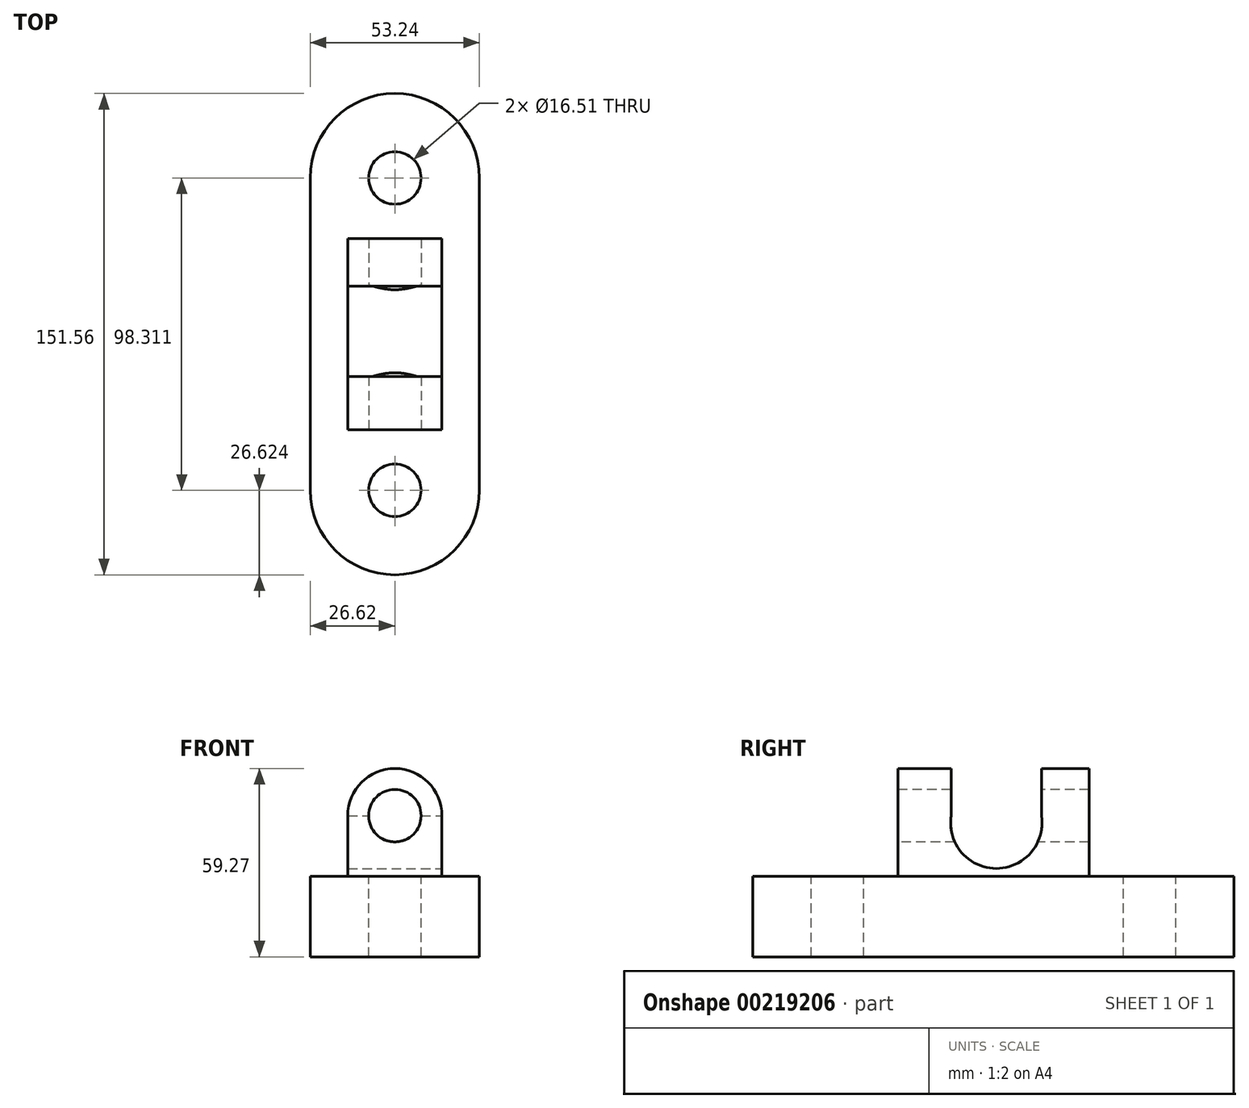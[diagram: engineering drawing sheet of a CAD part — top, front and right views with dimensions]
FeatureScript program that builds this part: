
annotation { "Feature Type Name" : "Feature", "Feature Type Description" : "" }
export const myFeature = defineFeature(function(context is Context, id is Id, definition is map)
    precondition{}
    {
        {
            var Q0;
            Q0=qCreatedBy(makeId("Top.planeOp"),FACE);
            var sketch = newSketch(context, id + "F0", { "sketchPlane" : qUnion([Q0])});
            skLineSegment(sketch, "E0.left", {"start": v(26.62, 49.16) * mm, "end": v(26.62, -49.16) * mm});
            skLineSegment(sketch, "E0.right", {"start": v(-26.62, 49.16) * mm, "end": v(-26.62, -49.16) * mm});
            skPoint(sketch, "E0.middle", {"position": v(0, 0) * mm});
            skArc(sketch, "E1", {"start": v(-26.62, -49.16) * mm, "mid": v(0, -75.78) * mm, "end": v(26.62, -49.16) * mm});
            skArc(sketch, "E2", {"start": v(-26.62, 49.16) * mm, "mid": v(0, 75.78) * mm, "end": v(26.62, 49.16) * mm});
            skSolve(sketch);
        }
        {
            var Q0;
            Q0 = qSketchRegion(id + "F0", true);
            extrude(context, id + "F1", {"entities" : qUnion([Q0]), "depth" : 25.4 * mm});
        }
        {
            var Q0;
            Q0=makeQuery(id+"F1.opExtrude","CAP_FACE",FACE,{"disambiguationData":[OSD([sQuery(id+"F0.wireOp",EDGE,"E0.left"),sQuery(id+"F0.wireOp",EDGE,"E0.right"),sQuery(id+"F0.wireOp",EDGE,"E1"),sQuery(id+"F0.wireOp",EDGE,"E2")])],"isStart":false});
            var sketch = newSketch(context, id + "F2", { "sketchPlane" : qUnion([Q0])});
            skCircle(sketch, "E3", {"center": v(0, -49.16) * mm, "radius": 9.2 * mm});
            skCircle(sketch, "E4.MirrorC", {"center": v(0, 49.16) * mm, "radius": 9.2 * mm});
            skSolve(sketch);
        }
        {
            var Q0;
            Q0=sQuery(id+"F2.wireOp",VERTEX,"E4.MirrorC.center");
            var Q1;
            Q1=sQuery(id+"F2.wireOp",VERTEX,"E3.center");
            var Q2;
            Q2=makeQuery(id+"F1.opExtrude","SWEPT_BODY",BODY,{"disambiguationData":[OSD([sQuery(id+"F0.wireOp",EDGE,"E0.left"),sQuery(id+"F0.wireOp",EDGE,"E0.right"),sQuery(id+"F0.wireOp",EDGE,"E1"),sQuery(id+"F0.wireOp",EDGE,"E2")])]});
            hole(context, id + "F3", {"style" : HoleStyle.SIMPLE, "endStyle" : HoleEndStyle.THROUGH, "holeDiameter" : 16.5 * mm, "locations" : qUnion([Q0, Q1]), "scope" : qUnion([Q2]), "isTappedThrough" : true});
        }
        {
            var Q0;
            Q0=makeQuery(id+"F1.opExtrude","CAP_FACE",FACE,{"disambiguationData":[OSD([sQuery(id+"F0.wireOp",EDGE,"E0.left"),sQuery(id+"F0.wireOp",EDGE,"E0.right"),sQuery(id+"F0.wireOp",EDGE,"E1"),sQuery(id+"F0.wireOp",EDGE,"E2")])],"isStart":false});
            var sketch = newSketch(context, id + "F4", { "sketchPlane" : qUnion([Q0])});
            skLineSegment(sketch, "E5.bottom", {"start": v(14.82, 30.1) * mm, "end": v(-14.82, 30.1) * mm});
            skLineSegment(sketch, "E5.top", {"start": v(14.82, -30.1) * mm, "end": v(-14.82, -30.1) * mm});
            skLineSegment(sketch, "E5.left", {"start": v(14.82, 30.1) * mm, "end": v(14.82, -30.1) * mm});
            skLineSegment(sketch, "E5.right", {"start": v(-14.82, 30.1) * mm, "end": v(-14.82, -30.1) * mm});
            skPoint(sketch, "E5.middle", {"position": v(0, 0) * mm});
            skSolve(sketch);
        }
        {
            var Q0;
            Q0 = qSketchRegion(id + "F4", true);
            extrude(context, id + "F5", {"entities" : qUnion([Q0]), "operationType" : NewBodyOperationType.ADD, "depth" : 38.1 * mm});
        }
        {
            var Q0;
            Q0=makeQuery(id+"F5.opExtrude","SWEPT_FACE",FACE,{"disambiguationData":[OSD([sQuery(id+"F4.wireOp",EDGE,"E5.top")])]});
            var sketch = newSketch(context, id + "F6", { "sketchPlane" : qUnion([Q0])});
            skLineSegment(sketch, "E6.bottom", {"start": v(14.82, 63.5) * mm, "end": v(-14.82, 63.5) * mm});
            skLineSegment(sketch, "E6.top", {"start": v(14.82, 25.4) * mm, "end": v(-14.82, 25.4) * mm});
            skLineSegment(sketch, "E6.left", {"start": v(14.82, 63.5) * mm, "end": v(14.82, 25.4) * mm});
            skLineSegment(sketch, "E6.right", {"start": v(-14.82, 63.5) * mm, "end": v(-14.82, 25.4) * mm});
            skPoint(sketch, "E6.middle", {"position": v(0, 44.45) * mm});
            skArc(sketch, "E7", {"start": v(14.82, 44.45) * mm, "mid": v(0, 59.27) * mm, "end": v(-14.82, 44.45) * mm});
            skSolve(sketch);
        }
        {
            var Q0;
            {var subQ0=sQuery(id+"F6.wireOp",EDGE,"E6.bottom");Q0=makeQuery(id+"F6.imprint","IMPRINT",FACE,{"disambiguationData":[TD([[makeQuery(id+"F6.imprint","IMPRINT",EDGE,{"derivedFrom":subQ0}),1.0]])]});}
            extrude(context, id + "F7", {"entities" : qUnion([Q0]), "operationType" : NewBodyOperationType.REMOVE, "oppositeDirection" : true, "depth" : 67.06 * mm});
        }
        {
            var Q0;
            Q0=makeQuery(id+"F5.opExtrude","SWEPT_FACE",FACE,{"disambiguationData":[OSD([sQuery(id+"F4.wireOp",EDGE,"E5.top")])]});
            var sketch = newSketch(context, id + "F8", { "sketchPlane" : qUnion([Q0])});
            skCircle(sketch, "E8", {"center": v(0, 44.45) * mm, "radius": 6.51 * mm});
            skSolve(sketch);
        }
        {
            var Q0;
            Q0=sQuery(id+"F8.wireOp",VERTEX,"E8.center");
            var Q1;
            Q1=makeQuery(id+"F1.opExtrude","SWEPT_BODY",BODY,{"disambiguationData":[OSD([sQuery(id+"F0.wireOp",EDGE,"E0.left"),sQuery(id+"F0.wireOp",EDGE,"E0.right"),sQuery(id+"F0.wireOp",EDGE,"E1"),sQuery(id+"F0.wireOp",EDGE,"E2")])]});
            hole(context, id + "F9", {"style" : HoleStyle.SIMPLE, "endStyle" : HoleEndStyle.THROUGH, "holeDiameter" : 16.5 * mm, "locations" : qUnion([Q0]), "scope" : qUnion([Q1]), "isTappedThrough" : true});
        }
        {
            var Q0;
            Q0=makeQuery(id+"F5.opExtrude","SWEPT_FACE",FACE,{"disambiguationData":[OSD([sQuery(id+"F4.wireOp",EDGE,"E5.left")])]});
            var sketch = newSketch(context, id + "F10", { "sketchPlane" : qUnion([Q0])});
            skPoint(sketch, "E9.centerSnap0", {"position": v(0, 44.45) * mm});
            skArc(sketch, "E10", {"start": v(-13.3, 44.45) * mm, "mid": v(0.9, 27.82) * mm, "end": v(15.12, 44.45) * mm});
            skLineSegment(sketch, "E11", {"start": v(-13.3, 44.45) * mm, "end": v(-13.3, 65.19) * mm});
            skLineSegment(sketch, "E12", {"start": v(-13.3, 65.19) * mm, "end": v(15.12, 65.19) * mm});
            skLineSegment(sketch, "E13", {"start": v(15.12, 65.19) * mm, "end": v(15.12, 44.45) * mm});
            skSolve(sketch);
        }
        {
            var Q0;
            Q0 = qSketchRegion(id + "F10", true);
            extrude(context, id + "F11", {"entities" : qUnion([Q0]), "operationType" : NewBodyOperationType.REMOVE, "endBound" : BoundingType.THROUGH_ALL, "oppositeDirection" : true, "depth" : 25.4 * mm});
        }
    });
